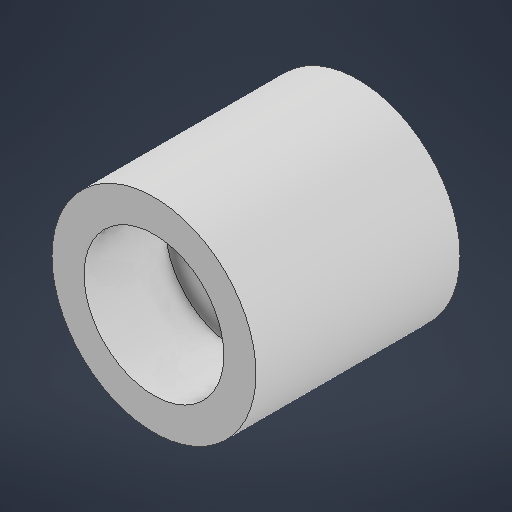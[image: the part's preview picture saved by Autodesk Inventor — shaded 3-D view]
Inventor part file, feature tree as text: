
AUTODESK INVENTOR PART (.ipt)
format: ipt  version: 2025.3 (Build 293356030, 356C)  size: 187,392 bytes
history: native  units: mm
features: extrude x3, sketch x2
ambient origin geometry x8: Origin, YZ Plane, XZ Plane, XY Plane, X Axis, Y Axis, Z Axis, Center Point
bodies: Solid1 (feature_tree)
feature tree (5):
  sketch  "Sketch1"  dims[d0=6.85mm d1=10.0mm]
  extrude  "Extrusion1"  Depth=10.0mm
  extrude  "Extrusion2"  Depth=6.0mm TaperAngle=0.0deg
  extrude  "Extrusion3"  Depth=5.0mm
  sketch  "Sketch2"  dims[d2=4.0mm d3=0.0mm d4=6.0mm d5=0.0mm d6=5.0mm d7=0.5mm d8=4.0mm d9=0.0mm]
